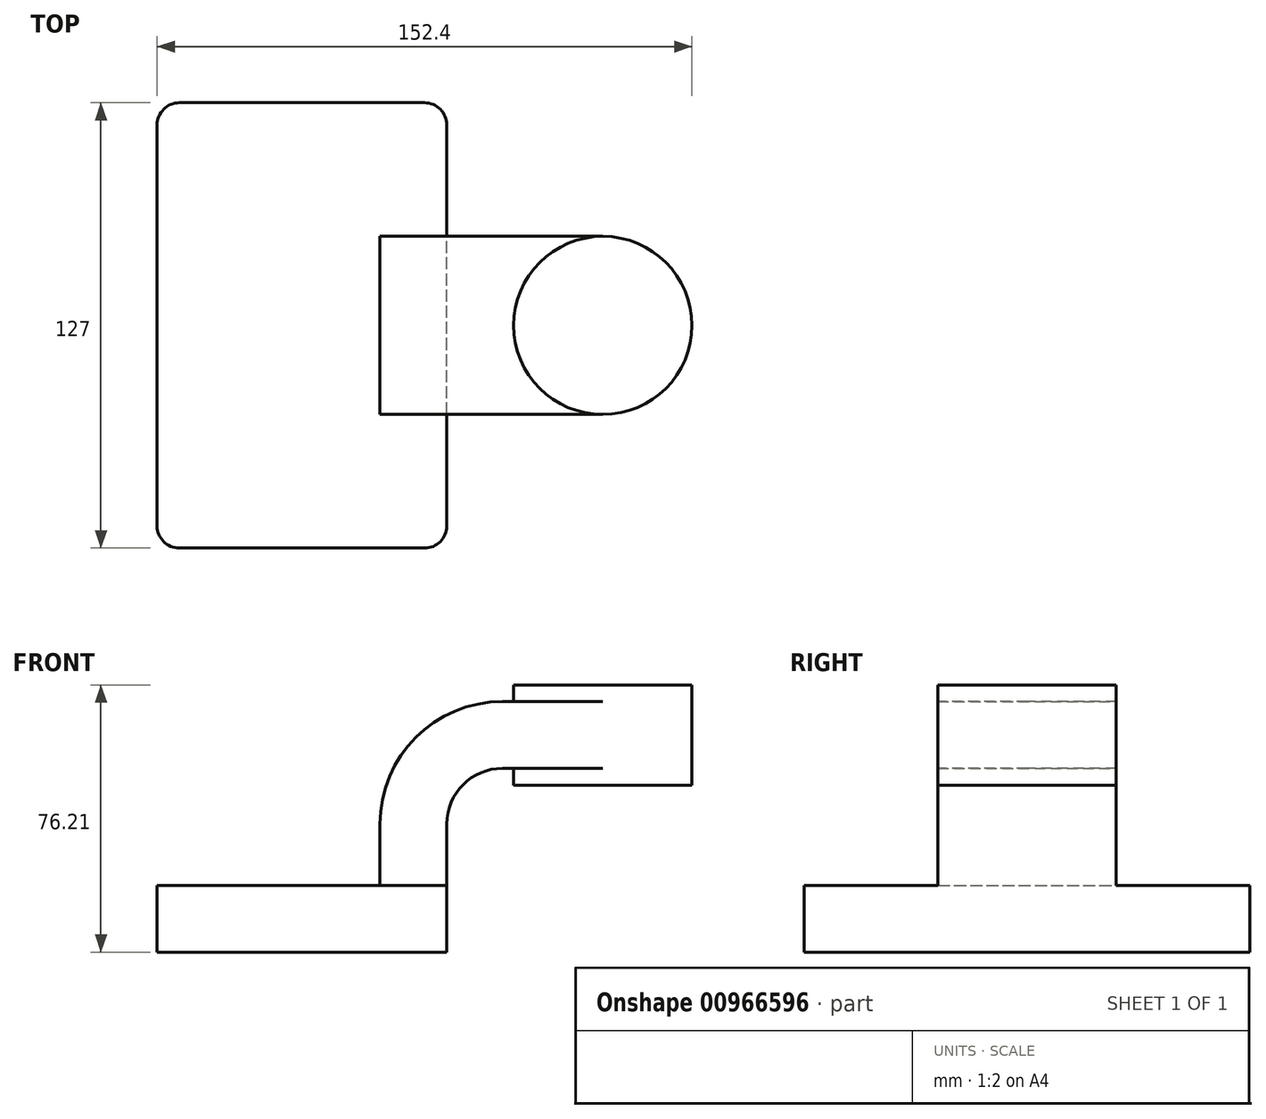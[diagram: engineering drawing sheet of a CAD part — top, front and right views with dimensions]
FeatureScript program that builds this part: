
annotation { "Feature Type Name" : "Feature", "Feature Type Description" : "" }
export const myFeature = defineFeature(function(context is Context, id is Id, definition is map)
    precondition{}
    {
        {
            var Q0;
            Q0=qCreatedBy(makeId("Front.planeOp"),FACE);
            var sketch = newSketch(context, id + "F0", { "sketchPlane" : qUnion([Q0])});
            skLineSegment(sketch, "E0.bottom", {"start": v(41.28, -9.52) * mm, "end": v(-41.28, -9.52) * mm});
            skLineSegment(sketch, "E0.top", {"start": v(41.28, 9.53) * mm, "end": v(-41.28, 9.53) * mm});
            skLineSegment(sketch, "E0.left", {"start": v(41.28, -9.52) * mm, "end": v(41.28, 9.53) * mm});
            skLineSegment(sketch, "E0.right", {"start": v(-41.28, -9.52) * mm, "end": v(-41.28, 9.53) * mm});
            skPoint(sketch, "E0.middle", {"position": v(0, 0) * mm});
            skLineSegment(sketch, "E1.bottom", {"start": v(111.12, 38.1) * mm, "end": v(60.32, 38.1) * mm});
            skLineSegment(sketch, "E1.top", {"start": v(111.12, 66.68) * mm, "end": v(60.32, 66.68) * mm});
            skLineSegment(sketch, "E1.left", {"start": v(111.12, 38.1) * mm, "end": v(111.12, 66.68) * mm});
            skLineSegment(sketch, "E1.right", {"start": v(60.32, 38.1) * mm, "end": v(60.32, 66.68) * mm});
            skPoint(sketch, "E1.middle", {"position": v(85.72, 52.39) * mm});
            skLineSegment(sketch, "E2", {"start": v(41.28, 9.53) * mm, "end": v(41.28, 27) * mm});
            skArc(sketch, "E3", {"start": v(41.28, 27) * mm, "mid": v(45.92, 38.23) * mm, "end": v(57.15, 42.88) * mm});
            skPoint(sketch, "E4.endSnap0", {"position": v(85.72, 38.1) * mm});
            skPoint(sketch, "E4.endSnap1", {"position": v(45.92, 38.23) * mm});
            skLineSegment(sketch, "E5", {"start": v(57.15, 42.88) * mm, "end": v(85.72, 42.88) * mm});
            skLineSegment(sketch, "E6.0", {"start": v(57.15, 61.93) * mm, "end": v(85.72, 61.93) * mm});
            skArc(sketch, "E6.1", {"start": v(22.23, 27) * mm, "mid": v(32.45, 51.7) * mm, "end": v(57.15, 61.93) * mm});
            skLineSegment(sketch, "E6.2", {"start": v(22.22, 9.53) * mm, "end": v(22.22, 27) * mm});
            skLineSegment(sketch, "E7", {"start": v(85.72, 38.1) * mm, "end": v(85.72, 66.68) * mm});
            skFitSpline(sketch, "E8", {"points": [v(-41.28, 9.52) * mm, v(57.15, 61.93) * mm], "startDerivative": vector(35.85, 112.37) * mm, "endDerivative": vector(131.1, -6.7) * mm});
            skSolve(sketch);
        }
        {
            var Q0;
            Q0=makeQuery(id+"F0.imprint","IMPRINT",FACE,{"disambiguationData":[TD([[makeQuery(id+"F0.imprint","IMPRINT",EDGE,{"derivedFrom":sQuery(id+"F0.wireOp",EDGE,"E0.bottom")}),-1.0]])]});
            extrude(context, id + "F1", {"entities" : qUnion([Q0]), "endBound" : BoundingType.SYMMETRIC, "depth" : 127 * mm, "offsetDistance" : 25.4 * mm});
        }
        {
            var Q0;
            {var subQ1=sQuery(id+"F0.wireOp",EDGE,"E2");Q0=makeQuery(id+"F0.imprint","IMPRINT",FACE,{"disambiguationData":[TD([[makeQuery(id+"F0.imprint","IMPRINT",EDGE,{"derivedFrom":subQ1}),1.0]])]});}
            var Q1;
            {var subQ0=sQuery(id+"F0.wireOp",EDGE,"E5");var subQ1=sQuery(id+"F0.wireOp",EDGE,"E1.right");var subQ2=makeQuery(id+"F0.imprint","INTERSECT",VERTEX,{"derivedFrom":[subQ1,subQ0]});Q1=makeQuery(id+"F0.imprint","IMPRINT",FACE,{"disambiguationData":[TD([[makeQuery(id+"F0.imprint","IMPRINT",EDGE,{"disambiguationData":[TD([[subQ2,-1.0]])],"derivedFrom":subQ1}),-1.0]])]});}
            extrude(context, id + "F2", {"entities" : qUnion([Q0, Q1]), "operationType" : NewBodyOperationType.ADD, "endBound" : BoundingType.SYMMETRIC, "depth" : 50.8 * mm, "offsetDistance" : 25.4 * mm});
        }
        {
            var Q0;
            Q0=makeQuery(id+"F0.imprint","IMPRINT",FACE,{"disambiguationData":[TD([[makeQuery(id+"F0.imprint","IMPRINT",EDGE,{"derivedFrom":sQuery(id+"F0.wireOp",EDGE,"E6.1")}),1.0]])]});
            extrude(context, id + "F3", {"entities" : qUnion([Q0]), "operationType" : NewBodyOperationType.ADD, "endBound" : BoundingType.SYMMETRIC, "depth" : 15.88 * mm, "offsetDistance" : 25.4 * mm});
        }
        {
            var Q0;
            {var subQ4=sQuery(id+"F0.wireOp",EDGE,"E1.left");Q0=makeQuery(id+"F0.imprint","IMPRINT",FACE,{"disambiguationData":[TD([[makeQuery(id+"F0.imprint","IMPRINT",EDGE,{"derivedFrom":subQ4}),1.0]])]});}
            var Q1;
            Q1=sQuery(id+"F0.wireOp",EDGE,"E7");
            revolve(context, id + "F4", {"operationType" : NewBodyOperationType.ADD, "surfaceOperationType" : NewSurfaceOperationType.NEW, "entities" : qUnion([Q0]), "axis" : qUnion([Q1]), "revolveType" : RevolveType.FULL});
        }
        {
            var Q0;
            Q0=makeQuery(id+"F1.opExtrude","CAP_EDGE",EDGE,{"disambiguationData":[OSD([sQuery(id+"F0.wireOp",EDGE,"E0.left")])],"isStart":false});
            var Q1;
            Q1=makeQuery(id+"F1.opExtrude","CAP_EDGE",EDGE,{"disambiguationData":[OSD([sQuery(id+"F0.wireOp",EDGE,"E0.left")])],"isStart":true});
            var Q2;
            Q2=makeQuery(id+"F1.opExtrude","CAP_EDGE",EDGE,{"disambiguationData":[OSD([sQuery(id+"F0.wireOp",EDGE,"E0.right")])],"isStart":true});
            var Q3;
            Q3=makeQuery(id+"F1.opExtrude","CAP_EDGE",EDGE,{"disambiguationData":[OSD([sQuery(id+"F0.wireOp",EDGE,"E0.right")])],"isStart":false});
            fillet(context, id + "F5", {"entities" : qUnion([Q0, Q1, Q2, Q3]), "radius" : 6.35 * mm, "tangentPropagation" : true, "allowEdgeOverflow" : false});
        }
    });
